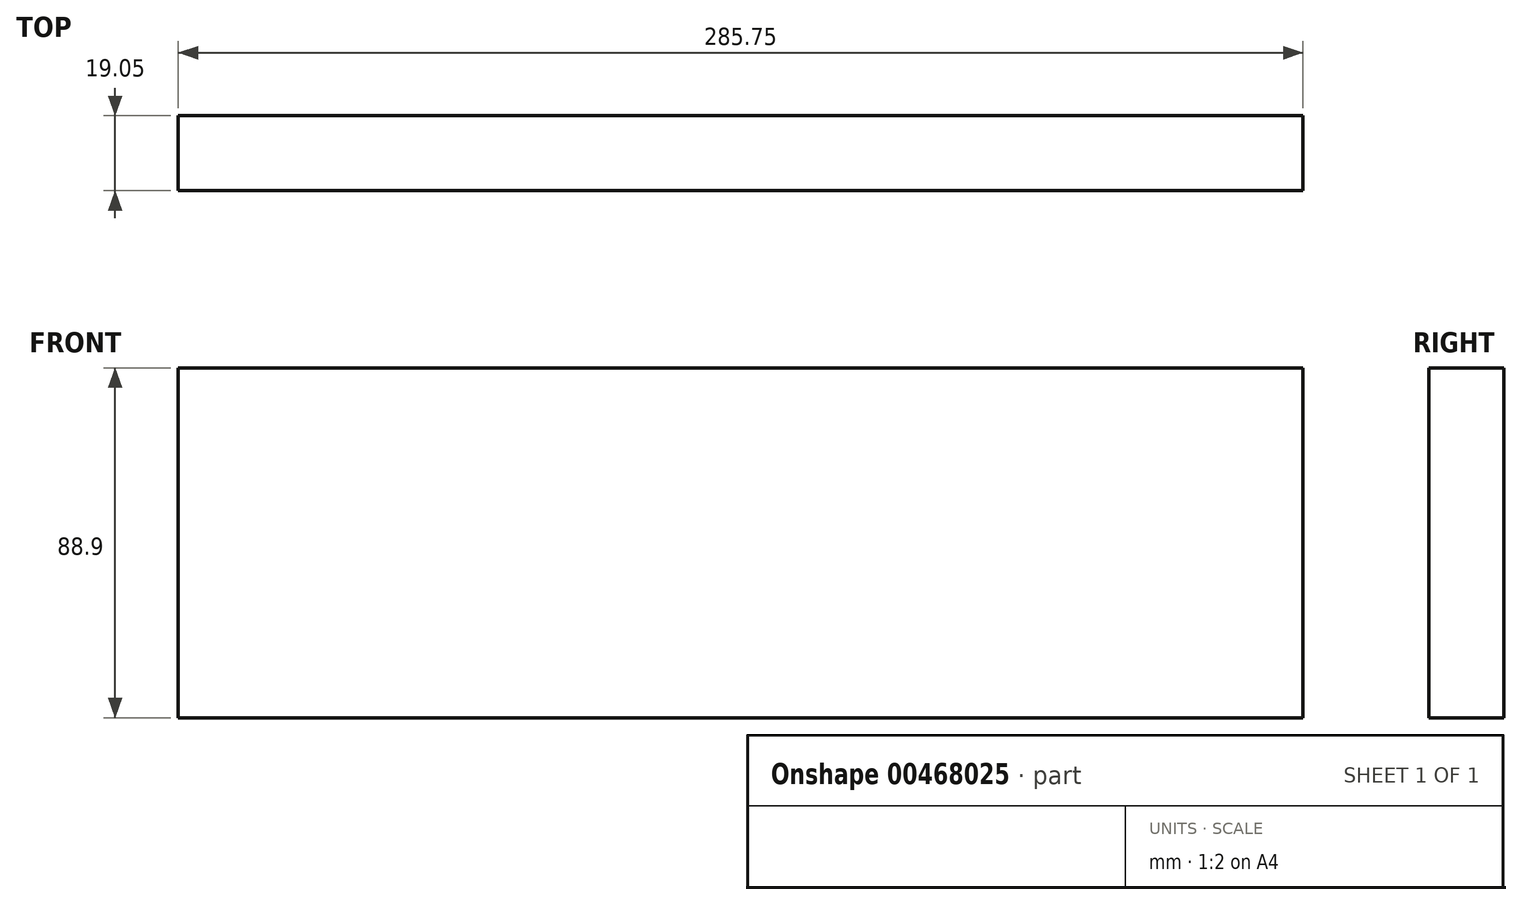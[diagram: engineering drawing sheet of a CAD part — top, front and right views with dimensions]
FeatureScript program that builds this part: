
annotation { "Feature Type Name" : "Feature", "Feature Type Description" : "" }
export const myFeature = defineFeature(function(context is Context, id is Id, definition is map)
    precondition{}
    {
        {
            var Q0;
            Q0=qCreatedBy(makeId("Right.planeOp"),FACE);
            var sketch = newSketch(context, id + "F0", { "sketchPlane" : qUnion([Q0])});
            skLineSegment(sketch, "E0.bottom", {"start": v(0, -25.18) * mm, "end": v(19.05, -25.18) * mm});
            skLineSegment(sketch, "E0.top", {"start": v(0, 63.72) * mm, "end": v(19.05, 63.72) * mm});
            skLineSegment(sketch, "E0.left", {"start": v(0, -25.18) * mm, "end": v(0, 63.72) * mm});
            skLineSegment(sketch, "E0.right", {"start": v(19.05, -25.18) * mm, "end": v(19.05, 63.72) * mm});
            skSolve(sketch);
        }
        {
            var Q0;
            Q0=makeQuery(id+"F0.imprint","IMPRINT",FACE,{"disambiguationData":[TD([[makeQuery(id+"F0.imprint","IMPRINT",EDGE,{"derivedFrom":sQuery(id+"F0.wireOp",EDGE,"E0.bottom")}),1.0]])]});
            extrude(context, id + "F1", {"entities" : qUnion([Q0]), "depth" : 285.75 * mm});
        }
    });
